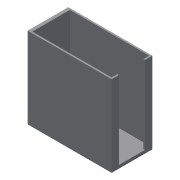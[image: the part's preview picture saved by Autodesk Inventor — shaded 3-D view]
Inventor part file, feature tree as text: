
AUTODESK INVENTOR PART (.ipt)
format: ipt  version: 2013 (Build 170138000, 138)  size: 116,224 bytes
history: native  units: in
note: dims shown in document units (in); Inventor stores cm internally (conversion verified against a paired STEP export)
features: extrude x3, sketch x3, mirror x1
ambient origin geometry x8: Origin, YZ Plane, XZ Plane, XY Plane, X Axis, Y Axis, Z Axis, Center Point
bodies: Solid1 (feature_tree)
feature tree (7):
  extrude  "Extrusion1"  Depth=1.1in
  extrude  "Extrusion2"  Depth=1.7in
  extrude  "Extrusion3"  Depth=0.035in
  mirror  "Mirror1"
  sketch  "Sketch2"  dims[d1=0.3in d2=1.1in]
  sketch  "Sketch5"  dims[d3=0.43in d4=1.7in]
  sketch  "Sketch6"  dims[d5=0.07in d6=0.035in d7=0.07in d10=1.77in d11=1.835in d12=0.82in d13=0.0in d14=0.57in d15=0.82in d16=0.0in d17=0.035in d18=0.0in]
